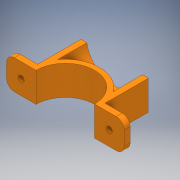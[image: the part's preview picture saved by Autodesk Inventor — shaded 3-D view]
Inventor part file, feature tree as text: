
AUTODESK INVENTOR PART (.ipt)
format: ipt  version: 2018 (Build 220112000, 112)  size: 152,064 bytes
history: native  units: mm
features: sketch x3, extrude x2, hole x1, mirror x1, plane x1, fillet x1
ambient origin geometry x8: Origin, YZ Plane, XZ Plane, XY Plane, X Axis, Y Axis, Z Axis, Center Point
bodies: Solid1 (feature_tree)
feature tree (9):
  extrude  "Extrusion1"  Depth=15.0mm TaperAngle=0.0deg
  hole  "Hole1"  [1 undecoded]
  mirror  "Mirror1"
  plane  "Work Plane1"
  extrude  "Extrusion2"  Depth=3.0mm
  fillet  "Fillet1"  Radius=3.0mm
  sketch  "Sketch1"  dims[d0=3.0mm d1=14.865mm d2=2.5mm d3=15.0mm d4=15.0mm d5=0.0mm]
  sketch  "Sketch2"  dims[d6=3.0mm d7=6.0mm d8=4.0mm d9=2.0mm d10=90.0deg d11=8.0mm d12=20.594885mm d13=25.0mm]
  sketch  "Sketch3"  dims[d14=3.0mm d15=3.0mm d16=3.0mm d17=15.0mm d18=0.0mm d19=4.0mm]
note: 1 required parameter value undecoded (feature->parameter linkage not recoverable at this tier; creation-order binding heuristic only, values carry confidence <= 0.55)
